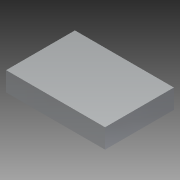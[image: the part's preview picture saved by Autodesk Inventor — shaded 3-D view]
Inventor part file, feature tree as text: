
AUTODESK INVENTOR PART (.ipt)
format: ipt  version: 2013 SP2 (Build 170200200, 200)  size: 68,608 bytes
history: native  units: mm
features: extrude x1, sketch x1
ambient origin geometry x8: Origin, YZ Plane, XZ Plane, XY Plane, X Axis, Y Axis, Z Axis, Center Point
bodies: Solid1 (feature_tree)
feature tree (2):
  extrude  "Extrusion1"  Depth=320.0mm
  sketch  "Sketch1"  dims[d0=460.0mm d1=320.0mm d2=90.0mm d3=0.0mm]
